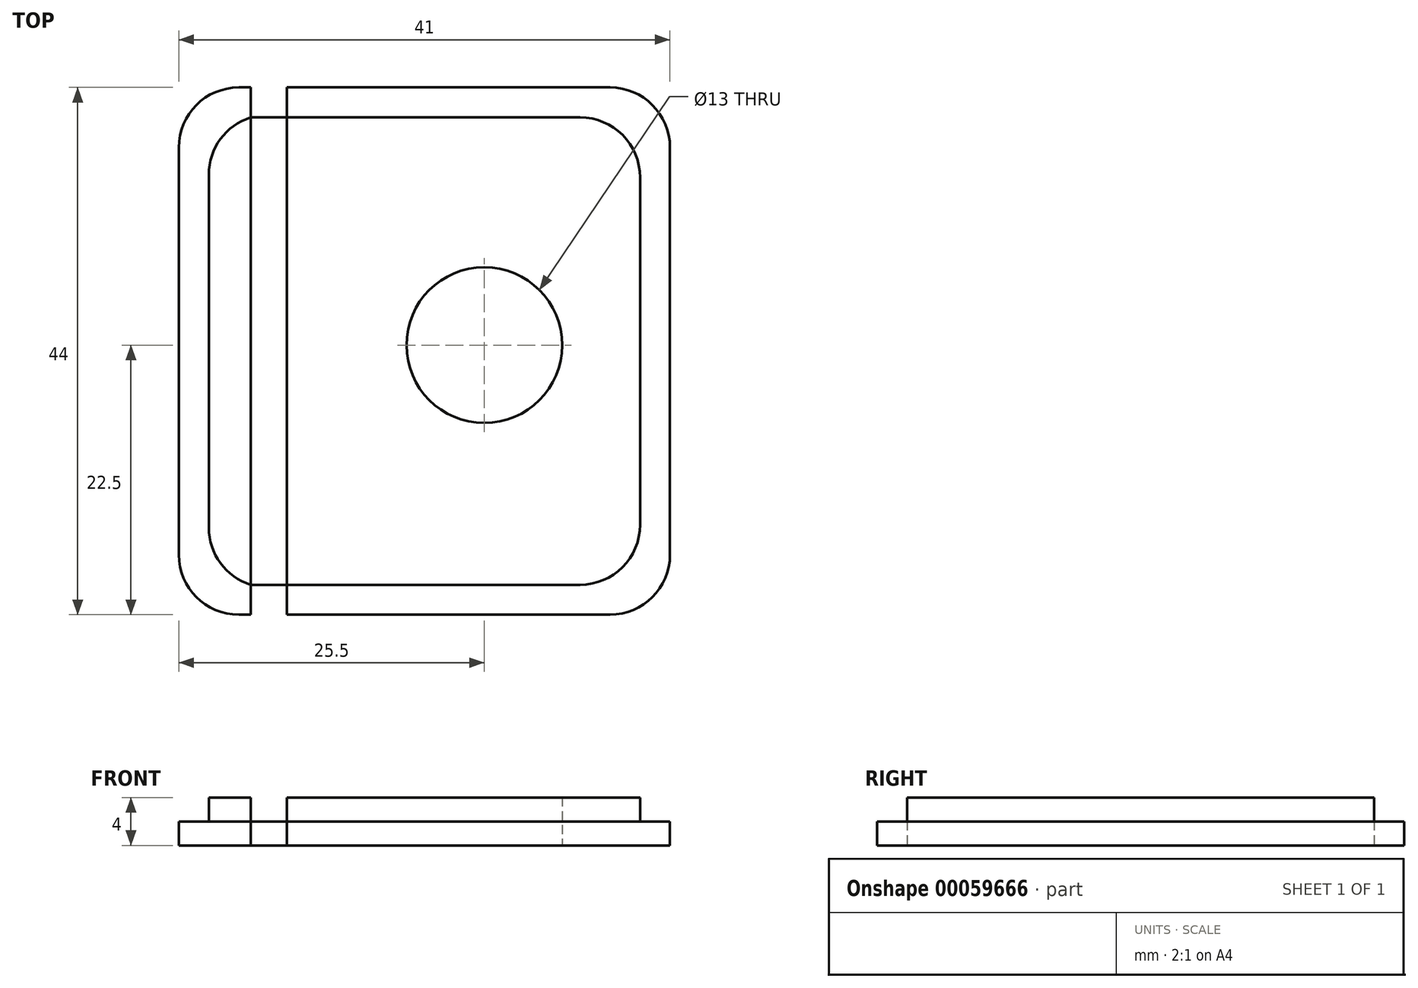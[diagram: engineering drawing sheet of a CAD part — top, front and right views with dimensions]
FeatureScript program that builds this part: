
annotation { "Feature Type Name" : "Feature", "Feature Type Description" : "" }
export const myFeature = defineFeature(function(context is Context, id is Id, definition is map)
    precondition{}
    {
        {
            var Q0;
            Q0=qCreatedBy(makeId("Top.planeOp"),FACE);
            var sketch = newSketch(context, id + "F0", { "sketchPlane" : qUnion([Q0])});
            skLineSegment(sketch, "E0.rect.bottom", {"start": v(20.5, 22) * mm, "end": v(-20.5, 22) * mm});
            skLineSegment(sketch, "E0.rect.top", {"start": v(20.5, -22) * mm, "end": v(-20.5, -22) * mm});
            skLineSegment(sketch, "E0.rect.left", {"start": v(20.5, 22) * mm, "end": v(20.5, -22) * mm});
            skLineSegment(sketch, "E0.rect.right", {"start": v(-20.5, 22) * mm, "end": v(-20.5, -22) * mm});
            skPoint(sketch, "E0.rect.middle", {"position": v(0, 0) * mm});
            skLineSegment(sketch, "E1.0", {"start": v(18, 19.5) * mm, "end": v(-18, 19.5) * mm});
            skLineSegment(sketch, "E1.1", {"start": v(18, 19.5) * mm, "end": v(18, -19.5) * mm});
            skLineSegment(sketch, "E1.2", {"start": v(18, -19.5) * mm, "end": v(-18, -19.5) * mm});
            skLineSegment(sketch, "E1.3", {"start": v(-18, 19.5) * mm, "end": v(-18, -19.5) * mm});
            skLineSegment(sketch, "E2.bottom", {"start": v(-14.5, 22) * mm, "end": v(-11.5, 22) * mm});
            skLineSegment(sketch, "E2.top", {"start": v(-14.5, -22) * mm, "end": v(-11.5, -22) * mm});
            skLineSegment(sketch, "E2.left", {"start": v(-14.5, 22) * mm, "end": v(-14.5, -22) * mm});
            skLineSegment(sketch, "E2.right", {"start": v(-11.5, 22) * mm, "end": v(-11.5, -22) * mm});
            skLineSegment(sketch, "E3", {"start": v(-20.5, 14.23) * mm, "end": v(-14.5, 14.23) * mm, "construction": true});
            skLineSegment(sketch, "E4", {"start": v(-14.5, 14.23) * mm, "end": v(-11.5, 14.23) * mm, "construction": true});
            skLineSegment(sketch, "E5", {"start": v(18, 0.5) * mm, "end": v(5, 0.5) * mm, "construction": true});
            skLineSegment(sketch, "E6", {"start": v(5, 0.5) * mm, "end": v(5, -19.5) * mm, "construction": true});
            skCircle(sketch, "E7", {"center": v(5, 0.5) * mm, "radius": 6.5 * mm});
            skSolve(sketch);
        }
        {
            var Q0;
            {var subQ4=sQuery(id+"F0.wireOp",EDGE,"E0.rect.left");Q0=makeQuery(id+"F0.imprint","IMPRINT",FACE,{"disambiguationData":[TD([[makeQuery(id+"F0.imprint","IMPRINT",EDGE,{"derivedFrom":subQ4}),-1.0]])]});}
            var Q1;
            {var subQ5=sQuery(id+"F0.wireOp",EDGE,"E2.bottom");Q1=makeQuery(id+"F0.imprint","IMPRINT",FACE,{"disambiguationData":[TD([[makeQuery(id+"F0.imprint","IMPRINT",EDGE,{"derivedFrom":subQ5}),-1.0]])]});}
            var Q2;
            {var subQ4=sQuery(id+"F0.wireOp",EDGE,"E0.rect.right");Q2=makeQuery(id+"F0.imprint","IMPRINT",FACE,{"disambiguationData":[TD([[makeQuery(id+"F0.imprint","IMPRINT",EDGE,{"derivedFrom":subQ4}),1.0]])]});}
            var Q3;
            {var subQ5=sQuery(id+"F0.wireOp",EDGE,"E2.top");Q3=makeQuery(id+"F0.imprint","IMPRINT",FACE,{"disambiguationData":[TD([[makeQuery(id+"F0.imprint","IMPRINT",EDGE,{"derivedFrom":subQ5}),1.0]])]});}
            var Q4;
            {var subQ0=sQuery(id+"F0.wireOp",EDGE,"E2.right");var subQ1=sQuery(id+"F0.wireOp",EDGE,"E1.0");var subQ2=makeQuery(id+"F0.imprint","INTERSECT",VERTEX,{"derivedFrom":[subQ1,subQ0]});Q4=makeQuery(id+"F0.imprint","IMPRINT",FACE,{"disambiguationData":[TD([[makeQuery(id+"F0.imprint","IMPRINT",EDGE,{"disambiguationData":[TD([[subQ2,-1.0]])],"derivedFrom":subQ1}),1.0]])]});}
            extrude(context, id + "F1", {"entities" : qUnion([Q0, Q1, Q2, Q3, Q4]), "depth" : 2 * mm});
        }
        {
            var Q0;
            {var subQ0=sQuery(id+"F0.wireOp",EDGE,"E1.3");Q0=makeQuery(id+"F0.imprint","IMPRINT",FACE,{"disambiguationData":[TD([[makeQuery(id+"F0.imprint","IMPRINT",EDGE,{"derivedFrom":subQ0}),1.0]])]});}
            var Q1;
            {var subQ0=sQuery(id+"F0.wireOp",EDGE,"E1.1");Q1=makeQuery(id+"F0.imprint","IMPRINT",FACE,{"disambiguationData":[TD([[makeQuery(id+"F0.imprint","IMPRINT",EDGE,{"derivedFrom":subQ0}),-1.0]])]});}
            extrude(context, id + "F2", {"entities" : qUnion([Q0, Q1]), "operationType" : NewBodyOperationType.ADD, "depth" : 4 * mm});
        }
        {
            var Q0;
            Q0=makeQuery(id+"F2.opExtrude","SWEPT_EDGE",EDGE,{"disambiguationData":[OSD([sQuery(id+"F0.wireOp",EDGE,"E1.0"),sQuery(id+"F0.wireOp",EDGE,"E1.3")])]});
            var Q1;
            Q1=makeQuery(id+"F2.opExtrude","SWEPT_EDGE",EDGE,{"disambiguationData":[OSD([sQuery(id+"F0.wireOp",EDGE,"E1.0"),sQuery(id+"F0.wireOp",EDGE,"E1.1")])]});
            var Q2;
            Q2=makeQuery(id+"F1.opExtrude","SWEPT_EDGE",EDGE,{"disambiguationData":[OSD([sQuery(id+"F0.wireOp",EDGE,"E0.rect.bottom"),sQuery(id+"F0.wireOp",EDGE,"E0.rect.right")])]});
            var Q3;
            Q3=makeQuery(id+"F1.opExtrude","SWEPT_EDGE",EDGE,{"disambiguationData":[OSD([sQuery(id+"F0.wireOp",EDGE,"E0.rect.top"),sQuery(id+"F0.wireOp",EDGE,"E0.rect.right")])]});
            var Q4;
            Q4=makeQuery(id+"F1.opExtrude","SWEPT_EDGE",EDGE,{"disambiguationData":[OSD([sQuery(id+"F0.wireOp",EDGE,"E0.rect.bottom"),sQuery(id+"F0.wireOp",EDGE,"E0.rect.left")])]});
            var Q5;
            Q5=makeQuery(id+"F2.opExtrude","SWEPT_EDGE",EDGE,{"disambiguationData":[OSD([sQuery(id+"F0.wireOp",EDGE,"E1.2"),sQuery(id+"F0.wireOp",EDGE,"E1.3")])]});
            var Q6;
            Q6=makeQuery(id+"F2.opExtrude","SWEPT_EDGE",EDGE,{"disambiguationData":[OSD([sQuery(id+"F0.wireOp",EDGE,"E1.1"),sQuery(id+"F0.wireOp",EDGE,"E1.2")])]});
            var Q7;
            Q7=makeQuery(id+"F1.opExtrude","SWEPT_EDGE",EDGE,{"disambiguationData":[OSD([sQuery(id+"F0.wireOp",EDGE,"E0.rect.top"),sQuery(id+"F0.wireOp",EDGE,"E0.rect.left")])]});
            fillet(context, id + "F3", {"entities" : qUnion([Q0, Q1, Q2, Q3, Q4, Q5, Q6, Q7]), "radius" : 5 * mm, "tangentPropagation" : true, "allowEdgeOverflow" : false});
        }
    });
